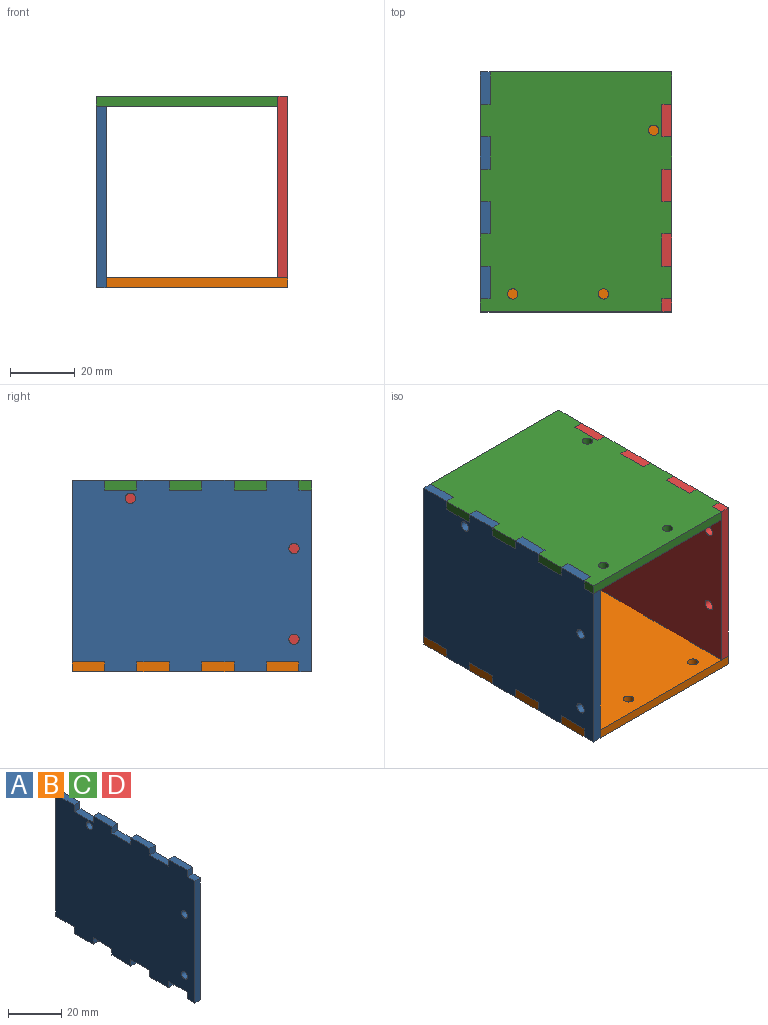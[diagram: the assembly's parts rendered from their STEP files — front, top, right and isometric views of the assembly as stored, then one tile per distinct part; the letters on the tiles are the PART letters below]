
ASSEMBLY  parts=4 mates=3
PART A: 37 faces, bbox 3x74x59 mm
  f0: plane 10x3mm, normal (0,0,-1), area 30mm2, adj f1,f34,f35,f36
  f1: plane 56x3mm, normal (0,1,0), area 168mm2, adj f0,f2,f35,f36
  f2: plane 10x3mm, normal (0,0,1), area 30mm2, adj f1,f3,f35,f36
  f3: plane 3x3mm, normal (0,-1,0), area 9mm2, adj f2,f4,f35,f36
  f4: plane 10x3mm, normal (0,0,1), area 30mm2, adj f3,f5,f35,f36
  f5: plane 3x3mm, normal (0,1,0), area 9mm2, adj f4,f6,f35,f36
  f6: plane 10x3mm, normal (0,0,1), area 30mm2, adj f5,f7,f35,f36
  f7: plane 3x3mm, normal (0,-1,0), area 9mm2, adj f6,f8,f35,f36
  f8: plane 10x3mm, normal (0,0,1), area 30mm2, adj f7,f9,f35,f36
  f9: plane 3x3mm, normal (0,1,0), area 9mm2, adj f8,f10,f35,f36
  f10: plane 10x3mm, normal (0,0,1), area 30mm2, adj f9,f11,f35,f36
  f11: plane 3x3mm, normal (0,-1,0), area 9mm2, adj f10,f12,f35,f36
  f12: plane 10x3mm, normal (0,0,1), area 30mm2, adj f11,f13,f35,f36
  f13: plane 3x3mm, normal (0,1,0), area 9mm2, adj f12,f14,f35,f36
  f14: plane 10x3mm, normal (0,0,1), area 30mm2, adj f13,f15,f35,f36
  f15: plane 3x3mm, normal (0,-1,0), area 9mm2, adj f14,f16,f35,f36
  f16: plane 4x3mm, normal (0,0,1), area 12mm2, adj f15,f17,f35,f36
  f17: plane 56x3mm, normal (0,-1,0), area 168mm2, adj f16,f18,f35,f36
  f18: plane 4x3mm, normal (0,0,-1), area 12mm2, adj f17,f19,f35,f36
  f19: plane 3x3mm, normal (0,1,0), area 9mm2, adj f18,f20,f35,f36
  f20: plane 10x3mm, normal (0,0,-1), area 30mm2, adj f19,f21,f35,f36
  f21: plane 3x3mm, normal (0,-1,0), area 9mm2, adj f20,f22,f35,f36
  f22: plane 10x3mm, normal (0,0,-1), area 30mm2, adj f21,f23,f35,f36
  f23: plane 3x3mm, normal (0,1,0), area 9mm2, adj f22,f24,f35,f36
  f24: plane 10x3mm, normal (0,0,-1), area 30mm2, adj f23,f25,f35,f36
  f25: plane 3x3mm, normal (0,-1,0), area 9mm2, adj f24,f26,f35,f36
  f26: plane 10x3mm, normal (0,0,-1), area 30mm2, adj f25,f27,f35,f36
  f27: plane 3x3mm, normal (0,1,0), area 9mm2, adj f26,f28,f35,f36
  f28: plane 10x3mm, normal (0,0,-1), area 30mm2, adj f27,f29,f35,f36
  f29: plane 3x3mm, normal (0,-1,0), area 9mm2, adj f28,f30,f35,f36
  f30: plane 10x3mm, normal (0,0,-1), area 30mm2, adj f29,f34,f35,f36
  f31: cylinder r=1.6mm len=3.2mm, axis (-1,0,0), area 30.2mm2, adj f35,f36
  f32: cylinder r=1.6mm len=3.2mm, axis (-1,0,0), area 30.2mm2, adj f35,f36
  f33: cylinder r=1.6mm len=3.2mm, axis (-1,0,0), area 30.2mm2, adj f35,f36
  f34: plane 3x3mm, normal (0,1,0), area 9mm2, adj f0,f30,f35,f36
  f35: plane 74x59mm, normal (1,0,0), area 4119.9mm2, adj f0,f1,f2,f3,f4,f5,f6,f7
  f36: plane 74x59mm, normal (-1,0,0), area 4119.9mm2, adj f0,f1,f2,f3,f4,f5,f6,f7
PART B: same geometry as A
PART C: same geometry as A
PART D: same geometry as A
PLACE A rot(axis=(0,-1,0),0deg) t=(-17.59,3.38,-33.97)mm
PLACE B rot(axis=(0,-1,0),90deg) t=(11.91,3.38,-63.47)mm
PLACE C rot(axis=(0,1,0),90deg) t=(11.91,3.38,-4.47)mm
PLACE D rot(axis=(0,-1,0),180deg) t=(41.41,3.38,-33.97)mm
MATE fastened A.f15 <-> C.f19  axis (0,-1,0) through (-16.09,-29.62,-5.97)mm
MATE fastened A.f34 <-> B.f3  axis (0,1,0) through (-16.09,30.38,-61.97)mm
MATE fastened B.f21 <-> D.f13  axis (0,-1,0) through (39.91,-19.62,-61.97)mm
